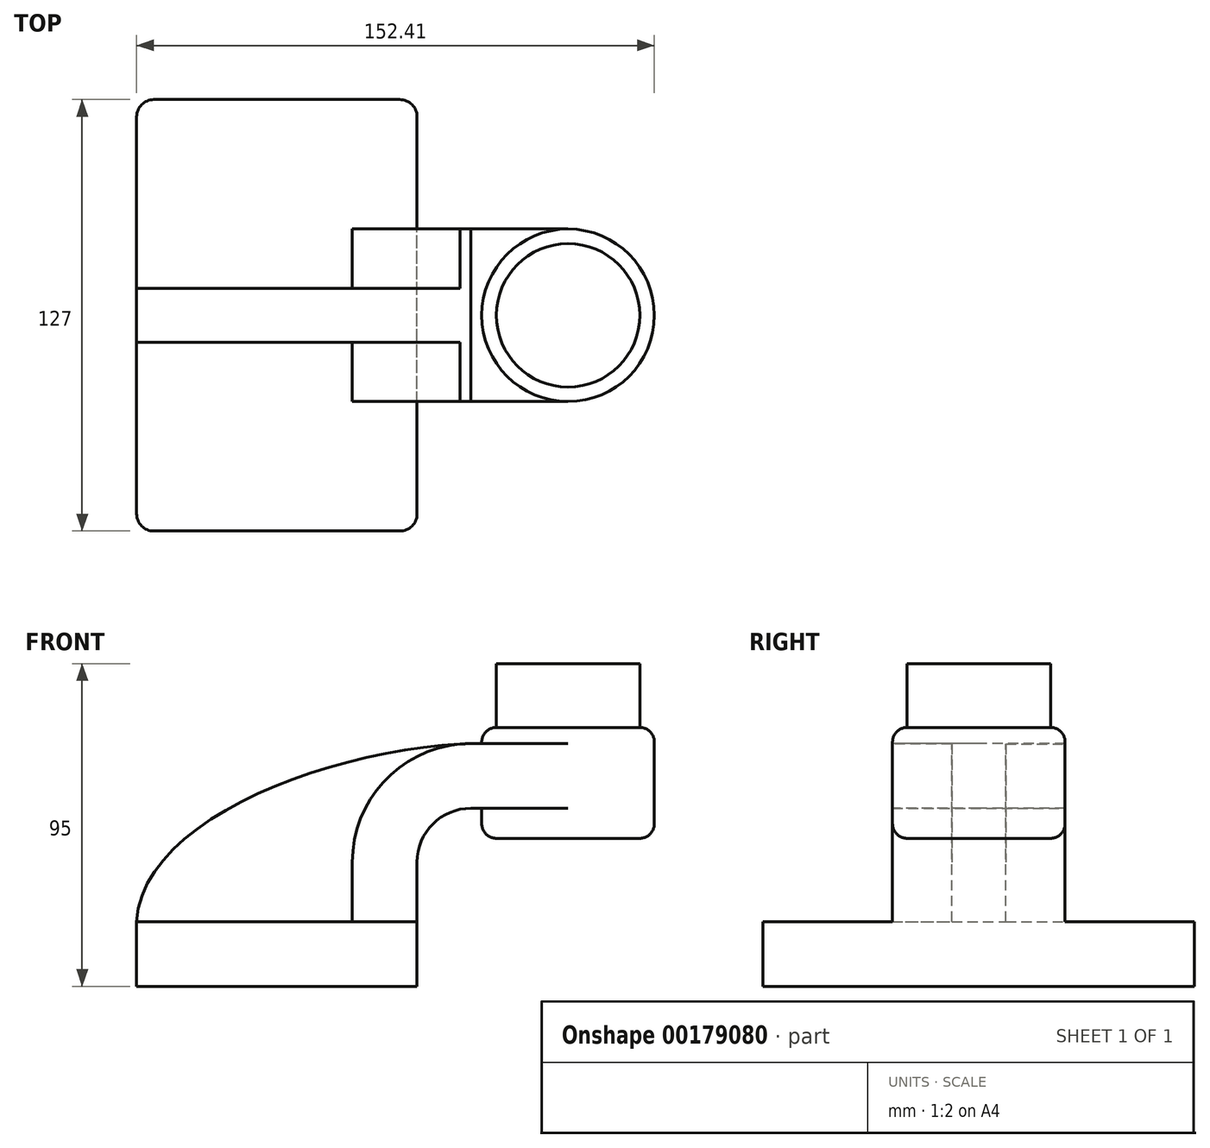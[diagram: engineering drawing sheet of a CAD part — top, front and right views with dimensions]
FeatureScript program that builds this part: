
annotation { "Feature Type Name" : "Feature", "Feature Type Description" : "" }
export const myFeature = defineFeature(function(context is Context, id is Id, definition is map)
    precondition{}
    {
        {
            var Q0;
            Q0=qCreatedBy(makeId("Front.planeOp"),FACE);
            var sketch = newSketch(context, id + "F0", { "sketchPlane" : qUnion([Q0])});
            skLineSegment(sketch, "E0.rect.bottom", {"start": v(-41.28, 9.52) * mm, "end": v(41.28, 9.52) * mm});
            skLineSegment(sketch, "E0.rect.top", {"start": v(-41.28, -9.52) * mm, "end": v(41.28, -9.52) * mm});
            skLineSegment(sketch, "E0.rect.left", {"start": v(-41.28, 9.52) * mm, "end": v(-41.28, -9.52) * mm});
            skLineSegment(sketch, "E0.rect.right", {"start": v(41.28, 9.52) * mm, "end": v(41.28, -9.52) * mm});
            skPoint(sketch, "E0.rect.middle", {"position": v(0, 0) * mm});
            skLineSegment(sketch, "E1", {"start": v(41.28, 9.52) * mm, "end": v(41.28, 27) * mm});
            skArc(sketch, "E2", {"start": v(41.28, 27) * mm, "mid": v(45.92, 38.23) * mm, "end": v(57.15, 42.88) * mm});
            skLineSegment(sketch, "E3", {"start": v(57.15, 42.88) * mm, "end": v(85.72, 42.88) * mm});
            skLineSegment(sketch, "E4.rect.bottom", {"start": v(60.32, 38.1) * mm, "end": v(111.12, 38.1) * mm});
            skLineSegment(sketch, "E4.rect.top", {"start": v(60.32, 66.68) * mm, "end": v(111.12, 66.68) * mm});
            skLineSegment(sketch, "E4.rect.left", {"start": v(60.32, 38.1) * mm, "end": v(60.32, 66.68) * mm});
            skLineSegment(sketch, "E4.rect.right", {"start": v(111.13, 38.1) * mm, "end": v(111.12, 66.68) * mm});
            skPoint(sketch, "E4.rect.middle", {"position": v(85.72, 52.39) * mm});
            skLineSegment(sketch, "E5.0", {"start": v(57.15, 61.93) * mm, "end": v(85.72, 61.93) * mm});
            skArc(sketch, "E5.1", {"start": v(22.23, 27) * mm, "mid": v(32.45, 51.7) * mm, "end": v(57.15, 61.93) * mm});
            skLineSegment(sketch, "E5.2", {"start": v(22.23, 9.52) * mm, "end": v(22.23, 27) * mm});
            skLineSegment(sketch, "E6", {"start": v(85.72, 38.1) * mm, "end": v(85.72, 66.68) * mm});
            skFitSpline(sketch, "E7", {"points": [v(-41.28, 9.53) * mm, v(57.15, 61.93) * mm], "startDerivative": vector(5.2, 92.34) * mm, "endDerivative": vector(120.92, 4.22) * mm});
            skSolve(sketch);
        }
        {
            var Q0;
            Q0=makeQuery(id+"F0.imprint","IMPRINT",FACE,{"disambiguationData":[TD([[makeQuery(id+"F0.imprint","IMPRINT",EDGE,{"derivedFrom":sQuery(id+"F0.wireOp",EDGE,"E0.rect.top")}),1.0]])]});
            extrude(context, id + "F1", {"entities" : qUnion([Q0]), "endBound" : BoundingType.SYMMETRIC, "depth" : 127 * mm});
        }
        {
            var Q0;
            {var subQ9=sQuery(id+"F0.wireOp",EDGE,"E1");Q0=makeQuery(id+"F0.imprint","IMPRINT",FACE,{"disambiguationData":[TD([[makeQuery(id+"F0.imprint","IMPRINT",EDGE,{"derivedFrom":subQ9}),1.0]])]});}
            var Q1;
            {var subQ0=sQuery(id+"F0.wireOp",EDGE,"E6");var subQ1=sQuery(id+"F0.wireOp",EDGE,"E3");var subQ2=makeQuery(id+"F0.imprint","INTERSECT",VERTEX,{"derivedFrom":[subQ1,subQ0]});Q1=makeQuery(id+"F0.imprint","IMPRINT",FACE,{"disambiguationData":[TD([[makeQuery(id+"F0.imprint","IMPRINT",EDGE,{"disambiguationData":[TD([[subQ2,1.0]])],"derivedFrom":subQ1}),1.0]])]});}
            extrude(context, id + "F2", {"entities" : qUnion([Q0, Q1]), "operationType" : NewBodyOperationType.ADD, "endBound" : BoundingType.SYMMETRIC, "depth" : 50.8 * mm});
        }
        {
            var Q0;
            {var subQ3=sQuery(id+"F0.wireOp",EDGE,"E5.2");Q0=makeQuery(id+"F0.imprint","IMPRINT",FACE,{"disambiguationData":[TD([[makeQuery(id+"F0.imprint","IMPRINT",EDGE,{"derivedFrom":subQ3}),1.0]])]});}
            extrude(context, id + "F3", {"entities" : qUnion([Q0]), "operationType" : NewBodyOperationType.ADD, "endBound" : BoundingType.SYMMETRIC, "depth" : 15.88 * mm});
        }
        {
            var Q0;
            {var subQ5=sQuery(id+"F0.wireOp",EDGE,"E4.rect.right");Q0=makeQuery(id+"F0.imprint","IMPRINT",FACE,{"disambiguationData":[TD([[makeQuery(id+"F0.imprint","IMPRINT",EDGE,{"derivedFrom":subQ5}),1.0]])]});}
            var Q1;
            Q1=sQuery(id+"F0.wireOp",EDGE,"E6");
            revolve(context, id + "F4", {"operationType" : NewBodyOperationType.ADD, "entities" : qUnion([Q0]), "axis" : qUnion([Q1]), "revolveType" : RevolveType.FULL});
        }
        {
            var Q0;
            Q0=makeQuery(id+"F1.opExtrude","CAP_EDGE",EDGE,{"disambiguationData":[OSD([sQuery(id+"F0.wireOp",EDGE,"E0.rect.right")])],"isStart":false});
            var Q1;
            Q1=makeQuery(id+"F1.opExtrude","CAP_EDGE",EDGE,{"disambiguationData":[OSD([sQuery(id+"F0.wireOp",EDGE,"E0.rect.left")])],"isStart":false});
            var Q2;
            Q2=makeQuery(id+"F1.opExtrude","CAP_EDGE",EDGE,{"disambiguationData":[OSD([sQuery(id+"F0.wireOp",EDGE,"E0.rect.right")])],"isStart":true});
            var Q3;
            Q3=makeQuery(id+"F1.opExtrude","CAP_EDGE",EDGE,{"disambiguationData":[OSD([sQuery(id+"F0.wireOp",EDGE,"E0.rect.left")])],"isStart":true});
            fillet(context, id + "F5", {"entities" : qUnion([Q0, Q1, Q2, Q3]), "radius" : 5.08 * mm, "tangentPropagation" : true, "allowEdgeOverflow" : false});
        }
        {
            var Q0;
            Q0=makeQuery(id+"F4.opRevolve","SWEPT_FACE",FACE,{"disambiguationData":[OSD([sQuery(id+"F0.wireOp",EDGE,"E4.rect.top")])]});
            var Q1;
            Q1=makeQuery(id+"F4.opRevolve","SWEPT_FACE",FACE,{"disambiguationData":[OSD([sQuery(id+"F0.wireOp",EDGE,"E4.rect.bottom")])]});
            extrude(context, id + "F6", {"entities" : qUnion([Q0, Q1]), "operationType" : NewBodyOperationType.ADD, "oppositeDirection" : true, "depth" : 4.08 * mm});
        }
        {
            var Q0;
            Q0=makeQuery(id+"F4.opRevolve","SWEPT_FACE",FACE,{"disambiguationData":[OSD([sQuery(id+"F0.wireOp",EDGE,"E4.rect.top")])]});
            var Q1;
            Q1=makeQuery(id+"F6.opExtrude","CAP_FACE",FACE,{"disambiguationData":[OSD([sQuery(id+"F0.wireOp",EDGE,"E4.rect.bottom")])],"isStart":false});
            fillet(context, id + "F7", {"entities" : qUnion([Q0, Q1]), "radius" : 4.3 * mm, "tangentPropagation" : true, "allowEdgeOverflow" : false});
        }
        {
            var Q0;
            Q0=makeQuery(id+"F4.opRevolve","SWEPT_FACE",FACE,{"disambiguationData":[OSD([sQuery(id+"F0.wireOp",EDGE,"E4.rect.top")])]});
            extrude(context, id + "F8", {"entities" : qUnion([Q0]), "operationType" : NewBodyOperationType.ADD, "depth" : 18.8 * mm});
        }
    });
